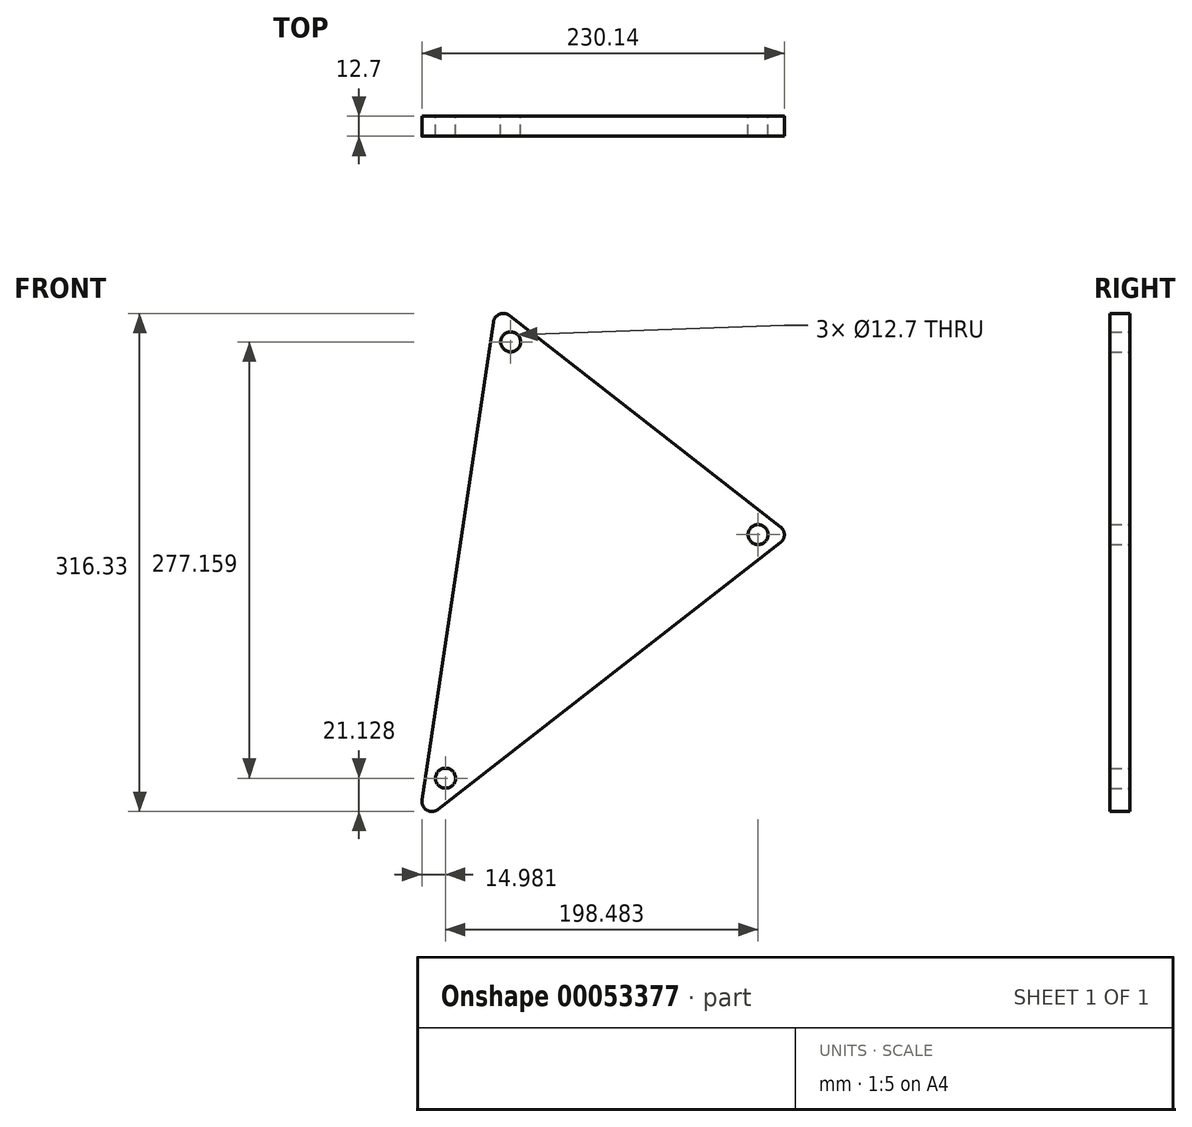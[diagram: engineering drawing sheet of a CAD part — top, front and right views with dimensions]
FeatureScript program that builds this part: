
annotation { "Feature Type Name" : "Feature", "Feature Type Description" : "" }
export const myFeature = defineFeature(function(context is Context, id is Id, definition is map)
    precondition{}
    {
        {
            var Q0;
            Q0=qCreatedBy(makeId("Front.planeOp"),FACE);
            var sketch = newSketch(context, id + "F0", { "sketchPlane" : qUnion([Q0])});
            skLineSegment(sketch, "E0", {"start": v(-76.24, 168.6) * mm, "end": v(95.87, 34.46) * mm});
            skLineSegment(sketch, "E1", {"start": v(95.87, 24.45) * mm, "end": v(-121.57, -145.04) * mm});
            skLineSegment(sketch, "E2", {"start": v(-131.76, -139.09) * mm, "end": v(-86.42, 164.54) * mm});
            skPoint(sketch, "E3.visualSharp", {"position": v(-84.82, 175.3) * mm});
            skArc(sketch, "E3.filletArc", {"start": v(-76.24, 168.6) * mm, "mid": v(-82.5, 169.5) * mm, "end": v(-86.42, 164.54) * mm});
            skPoint(sketch, "E4.visualSharp", {"position": v(102.3, 29.45) * mm});
            skArc(sketch, "E4.filletArc", {"start": v(95.87, 24.45) * mm, "mid": v(98.31, 29.45) * mm, "end": v(95.87, 34.46) * mm});
            skPoint(sketch, "E5.visualSharp", {"position": v(-134.1, -154.8) * mm});
            skArc(sketch, "E5.filletArc", {"start": v(-131.76, -139.09) * mm, "mid": v(-128.68, -145.51) * mm, "end": v(-121.57, -145.04) * mm});
            skCircle(sketch, "E6", {"center": v(-75.47, 151.9) * mm, "radius": 6.35 * mm});
            skCircle(sketch, "E7", {"center": v(-116.85, -125.25) * mm, "radius": 6.35 * mm});
            skCircle(sketch, "E8", {"center": v(81.63, 29.45) * mm, "radius": 6.35 * mm});
            skSolve(sketch);
        }
        {
            var Q0;
            Q0=makeQuery(id+"F0.imprint","IMPRINT",FACE,{"disambiguationData":[TD([[makeQuery(id+"F0.imprint","IMPRINT",EDGE,{"derivedFrom":sQuery(id+"F0.wireOp",EDGE,"E0")}),-1.0]])]});
            extrude(context, id + "F1", {"entities" : qUnion([Q0]), "depth" : 12.7 * mm});
        }
    });
